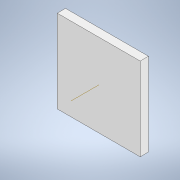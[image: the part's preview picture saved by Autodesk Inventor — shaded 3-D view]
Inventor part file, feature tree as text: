
AUTODESK INVENTOR PART (.ipt)
format: ipt  version: 2022 (Build 260153000, 153)  size: 95,232 bytes
history: native  units: mm
features: sketch x2, extrude x1, other x1
ambient origin geometry x8: Origin, YZ Plane, XZ Plane, XY Plane, X Axis, Y Axis, Z Axis, Center Point
bodies: Solid1 (feature_tree)
feature tree (4):
  extrude  "Extrusion1"  Depth=31.75mm
  sketch  "Sketch2"  dims[d2=3.175mm d3=0.0mm]
  other  "Work Axis1"
  sketch  "Sketch1"  dims[d0=31.75mm d1=31.75mm]
